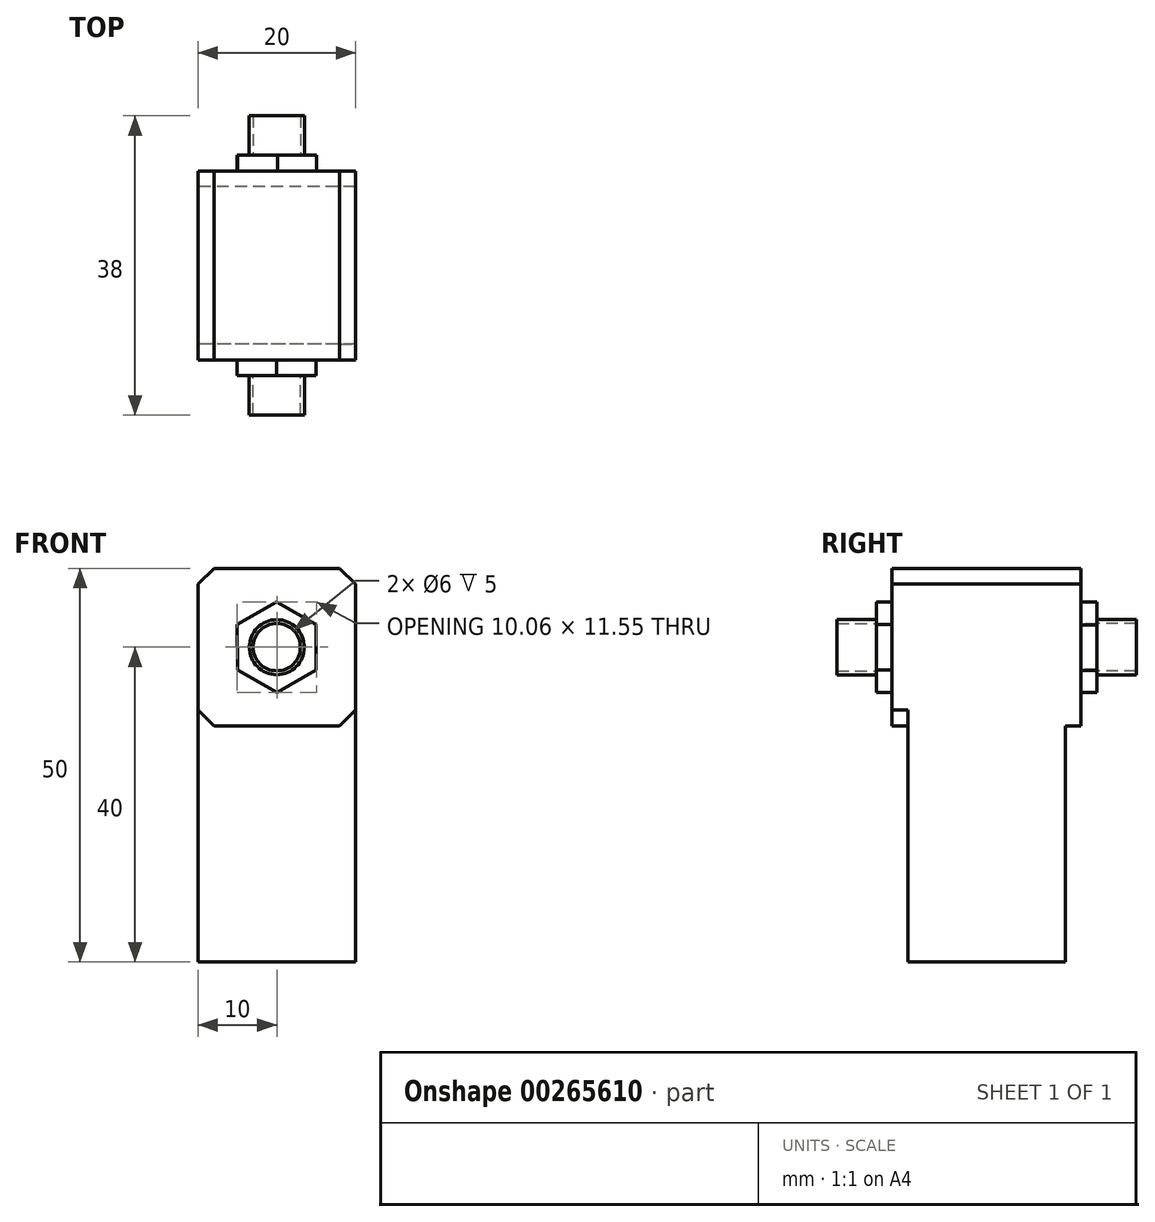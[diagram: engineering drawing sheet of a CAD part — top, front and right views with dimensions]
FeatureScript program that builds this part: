
annotation { "Feature Type Name" : "Feature", "Feature Type Description" : "" }
export const myFeature = defineFeature(function(context is Context, id is Id, definition is map)
    precondition{}
    {
        {
            var Q0;
            Q0=qCreatedBy(makeId("Front.planeOp"),FACE);
            var sketch = newSketch(context, id + "F0", { "sketchPlane" : qUnion([Q0])});
            skLineSegment(sketch, "E0.bottom", {"start": v(10, 25) * mm, "end": v(-10, 25) * mm});
            skLineSegment(sketch, "E0.top", {"start": v(10, -25) * mm, "end": v(-10, -25) * mm});
            skLineSegment(sketch, "E0.left", {"start": v(10, 25) * mm, "end": v(10, -25) * mm});
            skLineSegment(sketch, "E0.right", {"start": v(-10, 25) * mm, "end": v(-10, -25) * mm});
            skPoint(sketch, "E0.middle", {"position": v(0, 0) * mm});
            skSolve(sketch);
        }
        {
            var Q0;
            Q0=makeQuery(id+"F0.imprint","IMPRINT",FACE,{"disambiguationData":[TD([[makeQuery(id+"F0.imprint","IMPRINT",EDGE,{"derivedFrom":sQuery(id+"F0.wireOp",EDGE,"E0.bottom")}),1.0]])]});
            extrude(context, id + "F1", {"entities" : qUnion([Q0]), "depth" : 20 * mm});
        }
        {
            var Q0;
            Q0=makeQuery(id+"F1.opExtrude","CAP_FACE",FACE,{"disambiguationData":[OSD([sQuery(id+"F0.wireOp",EDGE,"E0.bottom"),sQuery(id+"F0.wireOp",EDGE,"E0.top"),sQuery(id+"F0.wireOp",EDGE,"E0.left"),sQuery(id+"F0.wireOp",EDGE,"E0.right")])],"isStart":false});
            var sketch = newSketch(context, id + "F2", { "sketchPlane" : qUnion([Q0])});
            skPoint(sketch, "E1", {"position": v(0, 15) * mm});
            skLineSegment(sketch, "E2.bottom", {"start": v(10, 25) * mm, "end": v(-10, 25) * mm});
            skLineSegment(sketch, "E2.top", {"start": v(10, 5) * mm, "end": v(-10, 5) * mm});
            skLineSegment(sketch, "E2.left", {"start": v(10, 25) * mm, "end": v(10, 5) * mm});
            skLineSegment(sketch, "E2.right", {"start": v(-10, 25) * mm, "end": v(-10, 5) * mm});
            skSolve(sketch);
        }
        {
            var Q0;
            Q0=makeQuery(id+"F2.imprint","IMPRINT",FACE,{"disambiguationData":[TD([[makeQuery(id+"F2.imprint","IMPRINT",EDGE,{"derivedFrom":sQuery(id+"F2.wireOp",EDGE,"E2.bottom")}),1.0]])]});
            extrude(context, id + "F3", {"entities" : qUnion([Q0]), "operationType" : NewBodyOperationType.ADD, "depth" : 2 * mm});
        }
        {
            var Q0;
            Q0=makeQuery(id+"F3.opExtrude","CAP_FACE",FACE,{"disambiguationData":[OSD([sQuery(id+"F2.wireOp",EDGE,"E2.bottom"),sQuery(id+"F2.wireOp",EDGE,"E2.top"),sQuery(id+"F2.wireOp",EDGE,"E2.left"),sQuery(id+"F2.wireOp",EDGE,"E2.right")])],"isStart":false});
            var sketch = newSketch(context, id + "F4", { "sketchPlane" : qUnion([Q0])});
            skPoint(sketch, "E3", {"position": v(0, 15) * mm});
            skLineSegment(sketch, "E4.bottom", {"start": v(7.5, 22.5) * mm, "end": v(-7.5, 22.5) * mm, "construction": true});
            skLineSegment(sketch, "E4.top", {"start": v(7.5, 7.5) * mm, "end": v(-7.5, 7.5) * mm, "construction": true});
            skLineSegment(sketch, "E4.left", {"start": v(7.5, 22.5) * mm, "end": v(7.5, 7.5) * mm, "construction": true});
            skLineSegment(sketch, "E4.right", {"start": v(-7.5, 22.5) * mm, "end": v(-7.5, 7.5) * mm, "construction": true});
            skCircle(sketch, "E5", {"center": v(-7.5, 22.5) * mm, "radius": 1.5 * mm});
            skCircle(sketch, "E6", {"center": v(7.5, 22.5) * mm, "radius": 1.5 * mm});
            skCircle(sketch, "E7", {"center": v(7.5, 7.5) * mm, "radius": 1.5 * mm});
            skCircle(sketch, "E8", {"center": v(-7.5, 7.5) * mm, "radius": 1.5 * mm});
            skCircle(sketch, "E9.cCircle", {"center": v(0, 15) * mm, "radius": 5 * mm, "construction": true});
            skLineSegment(sketch, "E9.0", {"start": v(-0.03, 20.77) * mm, "end": v(4.99, 17.91) * mm});
            skLineSegment(sketch, "E9.1", {"start": v(4.99, 17.91) * mm, "end": v(5.01, 12.14) * mm});
            skLineSegment(sketch, "E9.2", {"start": v(5.01, 12.14) * mm, "end": v(0.03, 9.23) * mm});
            skLineSegment(sketch, "E9.3", {"start": v(0.03, 9.23) * mm, "end": v(-4.99, 12.09) * mm});
            skLineSegment(sketch, "E9.4", {"start": v(-4.99, 12.09) * mm, "end": v(-5.01, 17.86) * mm});
            skLineSegment(sketch, "E9.5", {"start": v(-5.01, 17.86) * mm, "end": v(-0.03, 20.77) * mm});
            skPoint(sketch, "E9.0.midPoint", {"position": v(2.48, 19.34) * mm});
            skSolve(sketch);
        }
        {
            var Q0;
            Q0=makeQuery(id+"F4.imprint","IMPRINT",FACE,{"disambiguationData":[TD([[makeQuery(id+"F4.imprint","IMPRINT",EDGE,{"derivedFrom":sQuery(id+"F4.wireOp",EDGE,"E9.0")}),-1.0]])]});
            extrude(context, id + "F5", {"entities" : qUnion([Q0]), "operationType" : NewBodyOperationType.ADD, "depth" : 2 * mm});
        }
        {
            var Q0;
            Q0=makeQuery(id+"F5.opExtrude","CAP_FACE",FACE,{"disambiguationData":[OSD([sQuery(id+"F4.wireOp",EDGE,"E9.0"),sQuery(id+"F4.wireOp",EDGE,"E9.1"),sQuery(id+"F4.wireOp",EDGE,"E9.2"),sQuery(id+"F4.wireOp",EDGE,"E9.3"),sQuery(id+"F4.wireOp",EDGE,"E9.4"),sQuery(id+"F4.wireOp",EDGE,"E9.5")])],"isStart":false});
            var sketch = newSketch(context, id + "F6", { "sketchPlane" : qUnion([Q0])});
            skPoint(sketch, "E10", {"position": v(0, 15) * mm});
            skCircle(sketch, "E11", {"center": v(0, 15) * mm, "radius": 3.5 * mm});
            skCircle(sketch, "E12", {"center": v(0, 15) * mm, "radius": 3 * mm});
            skSolve(sketch);
        }
        {
            var Q0;
            Q0=makeQuery(id+"F6.imprint","IMPRINT",FACE,{"disambiguationData":[TD([[makeQuery(id+"F6.imprint","IMPRINT",EDGE,{"derivedFrom":sQuery(id+"F6.wireOp",EDGE,"E11")}),1.0]])]});
            extrude(context, id + "F7", {"entities" : qUnion([Q0]), "operationType" : NewBodyOperationType.ADD, "depth" : 5 * mm});
        }
        {
            var Q0;
            Q0=makeQuery(id+"F3.boolean.opBoolean","MERGE",EDGE,{"derivedFrom":[makeQuery(id+"F1.opExtrude","SWEPT_EDGE",EDGE,{"disambiguationData":[OSD([sQuery(id+"F0.wireOp",EDGE,"E0.bottom"),sQuery(id+"F0.wireOp",EDGE,"E0.right")])]}),makeQuery(id+"F3.opExtrude","SWEPT_EDGE",EDGE,{"disambiguationData":[OSD([sQuery(id+"F2.wireOp",EDGE,"E2.bottom"),sQuery(id+"F2.wireOp",EDGE,"E2.right")])]})]});
            var Q1;
            Q1=makeQuery(id+"F3.boolean.opBoolean","MERGE",EDGE,{"derivedFrom":[makeQuery(id+"F1.opExtrude","SWEPT_EDGE",EDGE,{"disambiguationData":[OSD([sQuery(id+"F0.wireOp",EDGE,"E0.bottom"),sQuery(id+"F0.wireOp",EDGE,"E0.left")])]}),makeQuery(id+"F3.opExtrude","SWEPT_EDGE",EDGE,{"disambiguationData":[OSD([sQuery(id+"F2.wireOp",EDGE,"E2.bottom"),sQuery(id+"F2.wireOp",EDGE,"E2.left")])]})]});
            var Q2;
            Q2=makeQuery(id+"F3.opExtrude","SWEPT_EDGE",EDGE,{"disambiguationData":[OSD([sQuery(id+"F0.wireOp",EDGE,"E0.right"),sQuery(id+"F2.wireOp",EDGE,"E2.top"),sQuery(id+"F2.wireOp",EDGE,"E2.right")])]});
            var Q3;
            Q3=makeQuery(id+"F3.opExtrude","SWEPT_EDGE",EDGE,{"disambiguationData":[OSD([sQuery(id+"F0.wireOp",EDGE,"E0.left"),sQuery(id+"F2.wireOp",EDGE,"E2.top"),sQuery(id+"F2.wireOp",EDGE,"E2.left")])]});
            chamfer(context, id + "F8", {"entities" : qUnion([Q0, Q1, Q2, Q3]), "width" : 2 * mm, "tangentPropagation" : true});
        }
        {
            var Q0;
            Q0=makeQuery(id+"F1.opExtrude","CAP_FACE",FACE,{"disambiguationData":[OSD([sQuery(id+"F0.wireOp",EDGE,"E0.bottom"),sQuery(id+"F0.wireOp",EDGE,"E0.top"),sQuery(id+"F0.wireOp",EDGE,"E0.left"),sQuery(id+"F0.wireOp",EDGE,"E0.right")])],"isStart":true});
            var sketch = newSketch(context, id + "F9", { "sketchPlane" : qUnion([Q0])});
            skPoint(sketch, "E13", {"position": v(0, 15) * mm});
            skLineSegment(sketch, "E14.bottom", {"start": v(10, 25) * mm, "end": v(-10, 25) * mm});
            skLineSegment(sketch, "E14.top", {"start": v(10, 5) * mm, "end": v(-10, 5) * mm});
            skLineSegment(sketch, "E14.left", {"start": v(10, 25) * mm, "end": v(10, 5) * mm});
            skLineSegment(sketch, "E14.right", {"start": v(-10, 25) * mm, "end": v(-10, 5) * mm});
            skSolve(sketch);
        }
        {
            var Q0;
            {var subQ7=sQuery(id+"F9.wireOp",EDGE,"E14.top");Q0=makeQuery(id+"F9.imprint","IMPRINT",FACE,{"disambiguationData":[TD([[makeQuery(id+"F9.imprint","IMPRINT",EDGE,{"derivedFrom":subQ7}),-1.0]])]});}
            extrude(context, id + "F10", {"entities" : qUnion([Q0]), "operationType" : NewBodyOperationType.ADD, "depth" : 2 * mm});
        }
        {
            var Q0;
            Q0=makeQuery(id+"F10.opExtrude","CAP_FACE",FACE,{"disambiguationData":[OSD([sQuery(id+"F0.wireOp",EDGE,"E0.bottom"),sQuery(id+"F0.wireOp",EDGE,"E0.top"),sQuery(id+"F0.wireOp",EDGE,"E0.left"),sQuery(id+"F0.wireOp",EDGE,"E0.right"),sQuery(id+"F2.wireOp",EDGE,"E2.bottom"),sQuery(id+"F2.wireOp",EDGE,"E2.left"),sQuery(id+"F2.wireOp",EDGE,"E2.right"),sQuery(id+"F9.wireOp",EDGE,"E14.bottom"),sQuery(id+"F9.wireOp",EDGE,"E14.top"),sQuery(id+"F9.wireOp",EDGE,"E14.left"),sQuery(id+"F9.wireOp",EDGE,"E14.right")])],"isStart":false});
            var sketch = newSketch(context, id + "F11", { "sketchPlane" : qUnion([Q0])});
            skPoint(sketch, "E15", {"position": v(0, 15) * mm});
            skCircle(sketch, "E16.cCircle", {"center": v(0, 15) * mm, "radius": 5 * mm, "construction": true});
            skLineSegment(sketch, "E16.0", {"start": v(-5.03, 17.83) * mm, "end": v(-0.06, 20.77) * mm});
            skLineSegment(sketch, "E16.1", {"start": v(-0.06, 20.77) * mm, "end": v(4.97, 17.94) * mm});
            skLineSegment(sketch, "E16.2", {"start": v(4.97, 17.94) * mm, "end": v(5.03, 12.17) * mm});
            skLineSegment(sketch, "E16.3", {"start": v(5.03, 12.17) * mm, "end": v(0.06, 9.23) * mm});
            skLineSegment(sketch, "E16.4", {"start": v(0.06, 9.23) * mm, "end": v(-4.97, 12.06) * mm});
            skLineSegment(sketch, "E16.5", {"start": v(-4.97, 12.06) * mm, "end": v(-5.03, 17.83) * mm});
            skPoint(sketch, "E16.0.midPoint", {"position": v(-2.55, 19.3) * mm});
            skSolve(sketch);
        }
        {
            var Q0;
            Q0=makeQuery(id+"F11.imprint","IMPRINT",FACE,{"disambiguationData":[TD([[makeQuery(id+"F11.imprint","IMPRINT",EDGE,{"derivedFrom":sQuery(id+"F11.wireOp",EDGE,"E16.0")}),-1.0]])]});
            extrude(context, id + "F12", {"entities" : qUnion([Q0]), "operationType" : NewBodyOperationType.ADD, "depth" : 2 * mm});
        }
        {
            var Q0;
            Q0=makeQuery(id+"F12.opExtrude","CAP_FACE",FACE,{"disambiguationData":[OSD([sQuery(id+"F11.wireOp",EDGE,"E16.0"),sQuery(id+"F11.wireOp",EDGE,"E16.1"),sQuery(id+"F11.wireOp",EDGE,"E16.2"),sQuery(id+"F11.wireOp",EDGE,"E16.3"),sQuery(id+"F11.wireOp",EDGE,"E16.4"),sQuery(id+"F11.wireOp",EDGE,"E16.5")])],"isStart":false});
            var sketch = newSketch(context, id + "F13", { "sketchPlane" : qUnion([Q0])});
            skPoint(sketch, "E17", {"position": v(0, 15) * mm});
            skCircle(sketch, "E18", {"center": v(0, 15) * mm, "radius": 3.5 * mm});
            skCircle(sketch, "E19", {"center": v(0, 15) * mm, "radius": 3 * mm});
            skSolve(sketch);
        }
        {
            var Q0;
            Q0=makeQuery(id+"F13.imprint","IMPRINT",FACE,{"disambiguationData":[TD([[makeQuery(id+"F13.imprint","IMPRINT",EDGE,{"derivedFrom":sQuery(id+"F13.wireOp",EDGE,"E18")}),1.0]])]});
            extrude(context, id + "F14", {"entities" : qUnion([Q0]), "operationType" : NewBodyOperationType.ADD, "depth" : 5 * mm});
        }
    });
